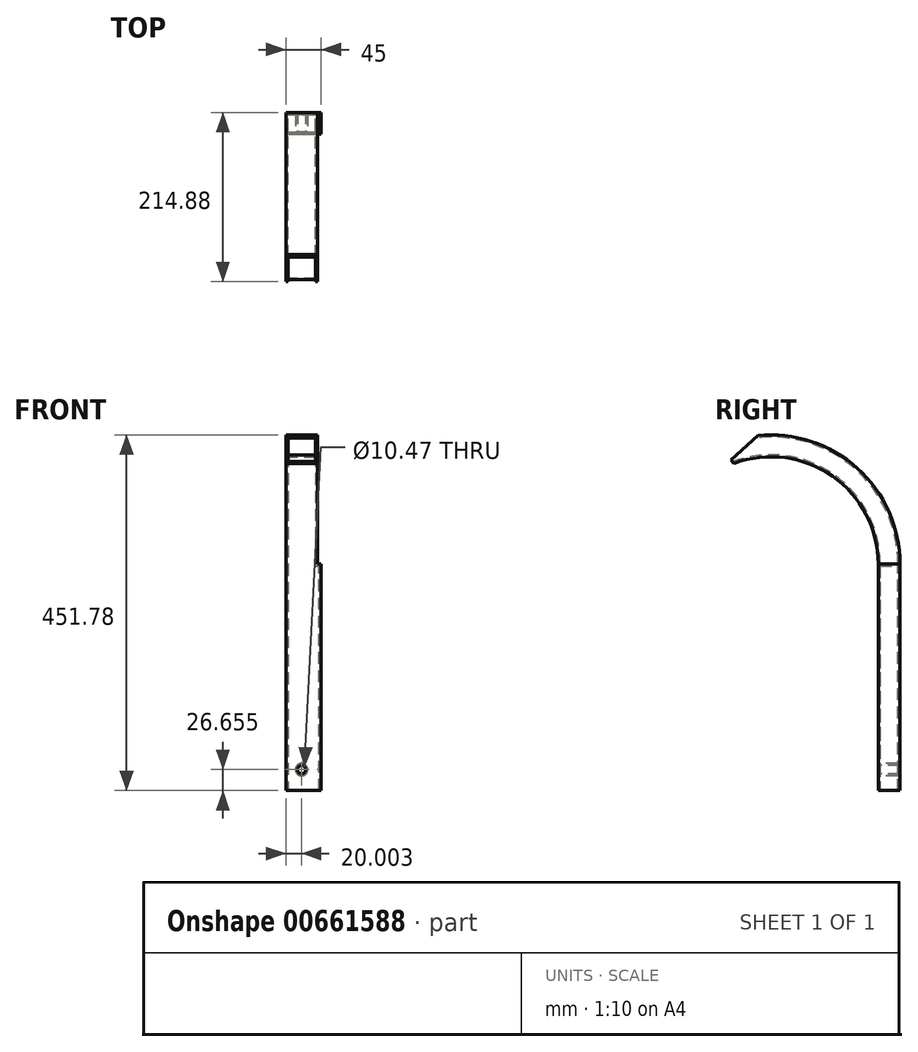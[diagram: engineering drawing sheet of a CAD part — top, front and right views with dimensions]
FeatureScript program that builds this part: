
annotation { "Feature Type Name" : "Feature", "Feature Type Description" : "" }
export const myFeature = defineFeature(function(context is Context, id is Id, definition is map)
    precondition{}
    {
        {
            var Q0;
            Q0=qCreatedBy(makeId("Front.planeOp"),FACE);
            var sketch = newSketch(context, id + "F0", { "sketchPlane" : qUnion([Q0])});
            skLineSegment(sketch, "E0.bottom", {"start": v(-20.98, -64.54) * mm, "end": v(59.02, -64.54) * mm});
            skLineSegment(sketch, "E0.top", {"start": v(-20.98, 335.46) * mm, "end": v(59.02, 335.46) * mm});
            skLineSegment(sketch, "E0.left", {"start": v(-20.98, -64.54) * mm, "end": v(-20.98, 335.46) * mm});
            skLineSegment(sketch, "E0.right", {"start": v(59.02, -64.54) * mm, "end": v(59.02, 335.46) * mm});
            skSolve(sketch);
        }
        {
            var Q0;
            Q0=makeQuery(id+"F0.imprint","IMPRINT",FACE,{"disambiguationData":[TD([[makeQuery(id+"F0.imprint","IMPRINT",EDGE,{"derivedFrom":sQuery(id+"F0.wireOp",EDGE,"E0.bottom")}),1.0]])]});
            extrude(context, id + "F1", {"entities" : qUnion([Q0]), "depth" : 300 * mm, "offsetDistance" : 25.4 * mm});
        }
        {
            var Q0;
            Q0=makeQuery(id+"F1.opExtrude","SWEPT_FACE",FACE,{"disambiguationData":[OSD([sQuery(id+"F0.wireOp",EDGE,"E0.left")])]});
            var sketch = newSketch(context, id + "F2", { "sketchPlane" : qUnion([Q0])});
            skLineSegment(sketch, "E1.1", {"start": v(300, -64.54) * mm, "end": v(0, -64.54) * mm});
            skLineSegment(sketch, "E2", {"start": v(40, -64.54) * mm, "end": v(40, 133.07) * mm});
            skLineSegment(sketch, "E3", {"start": v(218.3, 253.77) * mm, "end": v(248.43, 283.9) * mm});
            skPoint(sketch, "E4.orphan", {"position": v(0, 35.47) * mm});
            skArc(sketch, "E5.trimOffspring", {"start": v(218.3, 253.77) * mm, "mid": v(97.13, 240.73) * mm, "end": v(40, 133.07) * mm});
            skLineSegment(sketch, "E6.0", {"start": v(0, -64.54) * mm, "end": v(0, 133.07) * mm});
            skArc(sketch, "E6.1", {"start": v(248.43, 283.9) * mm, "mid": v(81.78, 278.39) * mm, "end": v(0, 133.07) * mm});
            skLineSegment(sketch, "E7.bottom", {"start": v(-14.01, 346.52) * mm, "end": v(324.59, 346.52) * mm});
            skLineSegment(sketch, "E7.top", {"start": v(-14.01, -79.57) * mm, "end": v(324.59, -79.57) * mm});
            skLineSegment(sketch, "E7.left", {"start": v(-14.01, 346.52) * mm, "end": v(-14.01, -79.57) * mm});
            skLineSegment(sketch, "E7.right", {"start": v(324.59, 346.52) * mm, "end": v(324.59, -79.57) * mm});
            skSolve(sketch);
        }
        {
            var Q0;
            {var subQ0=sQuery(id+"F2.wireOp",EDGE,"E2");Q0=makeQuery(id+"F2.imprint","IMPRINT",FACE,{"disambiguationData":[TD([[makeQuery(id+"F2.imprint","IMPRINT",EDGE,{"derivedFrom":subQ0}),-1.0]])]});}
            var Q1;
            {var subQ0=sQuery(id+"F2.wireOp",EDGE,"E6.0");Q1=makeQuery(id+"F2.imprint","IMPRINT",FACE,{"disambiguationData":[TD([[makeQuery(id+"F2.imprint","IMPRINT",EDGE,{"derivedFrom":subQ0}),1.0]])]});}
            extrude(context, id + "F3", {"entities" : qUnion([Q0, Q1]), "operationType" : NewBodyOperationType.REMOVE, "oppositeDirection" : true, "depth" : 108.97 * mm, "offsetDistance" : 25.4 * mm});
        }
        {
            var Q0;
            Q0=makeQuery(id+"F1.opExtrude","SWEPT_FACE",FACE,{"disambiguationData":[OSD([sQuery(id+"F0.wireOp",EDGE,"E0.bottom")])]});
            extrude(context, id + "F4", {"entities" : qUnion([Q0]), "operationType" : NewBodyOperationType.ADD, "depth" : 96.52 * mm, "offsetDistance" : 25.4 * mm});
        }
        {
            var Q0;
            {var subQ0=sQuery(id+"F2.wireOp",EDGE,"E2");var subQ1=sQuery(id+"F2.wireOp",EDGE,"E1.1");Q0=makeQuery(id+"F4.boolean.opBoolean","MERGE",FACE,{"derivedFrom":[makeQuery(id+"F3.boolean.opBoolean","COPY",FACE,{"derivedFrom":makeQuery(id+"F3.opExtrude","SWEPT_FACE",FACE,{"disambiguationData":[OSD([subQ0])]})}),makeQuery(id+"F4.opExtrude","SWEPT_FACE",FACE,{"disambiguationData":[OSD([subQ1,subQ0]),TDD([makeQuery(id+"F3.boolean.opBoolean","COPY",EDGE,{"derivedFrom":makeQuery(id+"F3.opExtrude","SWEPT_EDGE",EDGE,{"disambiguationData":[OSD([subQ1,subQ0])]})})])]})]});}
            var sketch = newSketch(context, id + "F5", { "sketchPlane" : qUnion([Q0])});
            skPoint(sketch, "E8.0", {"position": v(-20.98, -161.06) * mm});
            skPoint(sketch, "E9.0", {"position": v(59.02, -161.06) * mm});
            skLineSegment(sketch, "E10", {"start": v(19.02, -161.06) * mm, "end": v(19.02, 24.83) * mm});
            skCircle(sketch, "E11", {"center": v(19.02, -128.22) * mm, "radius": 5.23 * mm});
            skCircle(sketch, "E12", {"center": v(19.02, -73.97) * mm, "radius": 5.23 * mm});
            skSolve(sketch);
        }
        {
            var Q0;
            {var subQ0=sQuery(id+"F5.wireOp",EDGE,"E12");var subQ1=sQuery(id+"F5.wireOp",EDGE,"E10");var subQ2=makeQuery(id+"F5.imprint","INTERSECT",VERTEX,{"disambiguationData":[OD(0.0)],"derivedFrom":[subQ1,subQ0]});Q0=makeQuery(id+"F5.imprint","IMPRINT",FACE,{"disambiguationData":[TD([[makeQuery(id+"F5.imprint","IMPRINT",EDGE,{"disambiguationData":[TD([[subQ2,-1.0]])],"derivedFrom":subQ1}),-1.0]])]});}
            var Q1;
            {var subQ0=sQuery(id+"F5.wireOp",EDGE,"E12");var subQ1=sQuery(id+"F5.wireOp",EDGE,"E10");var subQ2=makeQuery(id+"F5.imprint","INTERSECT",VERTEX,{"disambiguationData":[OD(0.0)],"derivedFrom":[subQ1,subQ0]});Q1=makeQuery(id+"F5.imprint","IMPRINT",FACE,{"disambiguationData":[TD([[makeQuery(id+"F5.imprint","IMPRINT",EDGE,{"disambiguationData":[TD([[subQ2,-1.0]])],"derivedFrom":subQ1}),1.0]])]});}
            var Q2;
            {var subQ0=sQuery(id+"F5.wireOp",EDGE,"E11");var subQ1=sQuery(id+"F5.wireOp",EDGE,"E10");var subQ2=makeQuery(id+"F5.imprint","INTERSECT",VERTEX,{"disambiguationData":[OD(0.0)],"derivedFrom":[subQ1,subQ0]});Q2=makeQuery(id+"F5.imprint","IMPRINT",FACE,{"disambiguationData":[TD([[makeQuery(id+"F5.imprint","IMPRINT",EDGE,{"disambiguationData":[TD([[subQ2,-1.0]])],"derivedFrom":subQ1}),-1.0]])]});}
            var Q3;
            {var subQ0=sQuery(id+"F5.wireOp",EDGE,"E11");var subQ1=sQuery(id+"F5.wireOp",EDGE,"E10");var subQ2=makeQuery(id+"F5.imprint","INTERSECT",VERTEX,{"disambiguationData":[OD(0.0)],"derivedFrom":[subQ1,subQ0]});Q3=makeQuery(id+"F5.imprint","IMPRINT",FACE,{"disambiguationData":[TD([[makeQuery(id+"F5.imprint","IMPRINT",EDGE,{"disambiguationData":[TD([[subQ2,-1.0]])],"derivedFrom":subQ1}),1.0]])]});}
            extrude(context, id + "F6", {"entities" : qUnion([Q0, Q1, Q2, Q3]), "operationType" : NewBodyOperationType.REMOVE, "oppositeDirection" : true, "depth" : 46.23 * mm, "offsetDistance" : 25.4 * mm});
        }
        {
            var Q0;
            {var subQ0=sQuery(id+"F0.wireOp",EDGE,"E0.bottom");Q0=makeQuery(id+"F4.boolean.opBoolean","MERGE",FACE,{"derivedFrom":[makeQuery(id+"F1.opExtrude","CAP_FACE",FACE,{"disambiguationData":[OSD([subQ0,sQuery(id+"F0.wireOp",EDGE,"E0.top"),sQuery(id+"F0.wireOp",EDGE,"E0.left"),sQuery(id+"F0.wireOp",EDGE,"E0.right")])],"isStart":true}),makeQuery(id+"F4.opExtrude","SWEPT_FACE",FACE,{"disambiguationData":[OSD([subQ0])]})]});}
            var sketch = newSketch(context, id + "F7", { "sketchPlane" : qUnion([Q0])});
            skLineSegment(sketch, "E13", {"start": v(-19.02, -73.97) * mm, "end": v(-19.02, -175.55) * mm});
            skLineSegment(sketch, "E14", {"start": v(-19.02, -175.55) * mm, "end": v(5.98, -175.55) * mm});
            skLineSegment(sketch, "E15", {"start": v(5.98, -175.55) * mm, "end": v(5.98, 322.28) * mm});
            skLineSegment(sketch, "E16", {"start": v(5.98, 322.28) * mm, "end": v(-44.02, 322.28) * mm});
            skLineSegment(sketch, "E17", {"start": v(-44.02, 322.28) * mm, "end": v(-44.02, -175.55) * mm});
            skLineSegment(sketch, "E18", {"start": v(-44.02, -175.55) * mm, "end": v(-19.02, -175.55) * mm});
            skLineSegment(sketch, "E19.bottom", {"start": v(37.44, 348.2) * mm, "end": v(-87.02, 348.2) * mm});
            skLineSegment(sketch, "E19.top", {"start": v(37.44, -214.24) * mm, "end": v(-87.02, -214.24) * mm});
            skLineSegment(sketch, "E19.left", {"start": v(37.44, 348.2) * mm, "end": v(37.44, -214.24) * mm});
            skLineSegment(sketch, "E19.right", {"start": v(-87.02, 348.2) * mm, "end": v(-87.02, -214.24) * mm});
            skSolve(sketch);
        }
        {
            var Q0;
            {var subQ1=sQuery(id+"F0.wireOp",EDGE,"E0.bottom");var subQ4=sQuery(id+"F0.wireOp",EDGE,"E0.left");var subQ7=makeQuery(id+"F4.boolean.opBoolean","MERGE",EDGE,{"derivedFrom":[makeQuery(id+"F1.opExtrude","CAP_EDGE",EDGE,{"disambiguationData":[OSD([subQ4])],"isStart":true}),makeQuery(id+"F4.opExtrude","SWEPT_EDGE",EDGE,{"disambiguationData":[OSD([subQ1,subQ4])]})]});Q0=makeQuery(id+"F7.imprint","IMPRINT",FACE,{"disambiguationData":[TD([[makeQuery(id+"F7.imprint","IMPRINT",EDGE,{"derivedFrom":subQ7}),1.0]])]});}
            var Q1;
            {var subQ3=sQuery(id+"F0.wireOp",EDGE,"E0.bottom");var subQ6=sQuery(id+"F0.wireOp",EDGE,"E0.right");var subQ7=makeQuery(id+"F4.boolean.opBoolean","MERGE",EDGE,{"derivedFrom":[makeQuery(id+"F1.opExtrude","CAP_EDGE",EDGE,{"disambiguationData":[OSD([subQ6])],"isStart":true}),makeQuery(id+"F4.opExtrude","SWEPT_EDGE",EDGE,{"disambiguationData":[OSD([subQ3,subQ6])]})]});Q1=makeQuery(id+"F7.imprint","IMPRINT",FACE,{"disambiguationData":[TD([[makeQuery(id+"F7.imprint","IMPRINT",EDGE,{"derivedFrom":subQ7}),-1.0]])]});}
            var Q2;
            {var subQ9=sQuery(id+"F7.wireOp",EDGE,"E14");Q2=makeQuery(id+"F7.imprint","IMPRINT",FACE,{"disambiguationData":[TD([[makeQuery(id+"F7.imprint","IMPRINT",EDGE,{"derivedFrom":subQ9}),-1.0]])]});}
            extrude(context, id + "F8", {"entities" : qUnion([Q0, Q1, Q2]), "operationType" : NewBodyOperationType.REMOVE, "oppositeDirection" : true, "depth" : 391.16 * mm, "offsetDistance" : 25.4 * mm});
        }
        {
            var Q0;
            Q0=makeQuery(id+"F8.boolean.opBoolean","COPY",FACE,{"derivedFrom":makeQuery(id+"F8.opExtrude","SWEPT_FACE",FACE,{"disambiguationData":[OSD([sQuery(id+"F7.wireOp",EDGE,"E17")])]})});
            var sketch = newSketch(context, id + "F9", { "sketchPlane" : qUnion([Q0])});
            skLineSegment(sketch, "E20.0.0", {"start": v(-248.43, 283.9) * mm, "end": v(-218.3, 253.77) * mm});
            skArc(sketch, "E20.0.1", {"start": v(-218.3, 253.77) * mm, "mid": v(-97.13, 240.73) * mm, "end": v(-40, 133.07) * mm});
            skLineSegment(sketch, "E20.0.2", {"start": v(-40, 133.07) * mm, "end": v(-40, -161.06) * mm});
            skLineSegment(sketch, "E20.0.3", {"start": v(-40, -161.06) * mm, "end": v(0, -161.06) * mm});
            skLineSegment(sketch, "E20.0.4", {"start": v(0, -161.06) * mm, "end": v(0, 133.07) * mm});
            skArc(sketch, "E20.0.5", {"start": v(-248.43, 283.9) * mm, "mid": v(-81.78, 278.39) * mm, "end": v(0, 133.07) * mm});
            skArc(sketch, "E21.0", {"start": v(-245.5, 278.26) * mm, "mid": v(-85.07, 272.96) * mm, "end": v(-6.35, 133.07) * mm});
            skArc(sketch, "E22.0", {"start": v(-222.64, 264.61) * mm, "mid": v(-90.58, 250.4) * mm, "end": v(-28.32, 133.07) * mm});
            skLineSegment(sketch, "E23.0", {"start": v(-28.32, 133.07) * mm, "end": v(-28.32, -161.06) * mm});
            skLineSegment(sketch, "E24.0", {"start": v(-33.83, -154.88) * mm, "end": v(-6.17, -154.88) * mm});
            skArc(sketch, "E24.1", {"start": v(-237.95, 282.14) * mm, "mid": v(-81.38, 270.86) * mm, "end": v(-6.17, 133.07) * mm});
            skLineSegment(sketch, "E24.2", {"start": v(-237.95, 282.14) * mm, "end": v(-216.77, 260.96) * mm});
            skLineSegment(sketch, "E24.3", {"start": v(-6.17, -154.88) * mm, "end": v(-6.17, 133.07) * mm});
            skArc(sketch, "E24.4", {"start": v(-216.77, 260.96) * mm, "mid": v(-91.98, 244.68) * mm, "end": v(-33.83, 133.07) * mm});
            skLineSegment(sketch, "E24.5", {"start": v(-33.83, 133.07) * mm, "end": v(-33.83, -154.88) * mm});
            skSolve(sketch);
        }
        {
            var Q0;
            {var subQ2=sQuery(id+"F9.wireOp",EDGE,"E20.0.4");Q0=makeQuery(id+"F9.imprint","IMPRINT",FACE,{"disambiguationData":[TD([[makeQuery(id+"F9.imprint","IMPRINT",EDGE,{"derivedFrom":subQ2}),-1.0]])]});}
            var Q1;
            {var subQ13=sQuery(id+"F9.wireOp",EDGE,"E20.0.1");Q1=makeQuery(id+"F9.imprint","IMPRINT",FACE,{"disambiguationData":[TD([[makeQuery(id+"F9.imprint","IMPRINT",EDGE,{"derivedFrom":subQ13}),1.0]])]});}
            var Q2;
            {var subQ0=sQuery(id+"F9.wireOp",EDGE,"E24.4");Q2=makeQuery(id+"F9.imprint","IMPRINT",FACE,{"disambiguationData":[TD([[makeQuery(id+"F9.imprint","IMPRINT",EDGE,{"derivedFrom":subQ0}),1.0]])]});}
            extrude(context, id + "F10", {"entities" : qUnion([Q0, Q1, Q2]), "operationType" : NewBodyOperationType.REMOVE, "oppositeDirection" : true, "depth" : 73.66 * mm, "offsetDistance" : 25.4 * mm});
        }
        {
            var Q0;
            Q0=makeQuery(id+"F10.boolean.opBoolean","COPY",FACE,{"derivedFrom":makeQuery(id+"F10.opExtrude","SWEPT_FACE",FACE,{"disambiguationData":[OSD([sQuery(id+"F9.wireOp",EDGE,"E24.3")])]})});
            var sketch = newSketch(context, id + "F11", { "sketchPlane" : qUnion([Q0])});
            skLineSegment(sketch, "E25", {"start": v(-19.02, -128.22) * mm, "end": v(0.98, -128.22) * mm});
            skLineSegment(sketch, "E26", {"start": v(-19.02, -73.97) * mm, "end": v(-39.02, -73.97) * mm});
            skLineSegment(sketch, "E27.bottom", {"start": v(0.98, -172.53) * mm, "end": v(-39.02, -172.53) * mm});
            skLineSegment(sketch, "E27.top", {"start": v(0.98, 334.83) * mm, "end": v(-39.02, 334.83) * mm});
            skLineSegment(sketch, "E27.left", {"start": v(0.98, -172.53) * mm, "end": v(0.98, 334.83) * mm});
            skLineSegment(sketch, "E27.right", {"start": v(-39.02, -172.53) * mm, "end": v(-39.02, 334.83) * mm});
            skLineSegment(sketch, "E28.bottom", {"start": v(-65, 352.61) * mm, "end": v(27.95, 352.61) * mm});
            skLineSegment(sketch, "E28.top", {"start": v(-65, -187.26) * mm, "end": v(27.95, -187.26) * mm});
            skLineSegment(sketch, "E28.left", {"start": v(-65, 352.61) * mm, "end": v(-65, -187.26) * mm});
            skLineSegment(sketch, "E28.right", {"start": v(27.95, 352.61) * mm, "end": v(27.95, -187.26) * mm});
            skSolve(sketch);
        }
        {
            var Q0;
            {var subQ0=sQuery(id+"F9.wireOp",EDGE,"E24.3");var subQ1=makeQuery(id+"F10.boolean.opBoolean","INTERSECT",EDGE,{"derivedFrom":[makeQuery(id+"F8.boolean.opBoolean","COPY",FACE,{"derivedFrom":makeQuery(id+"F8.opExtrude","SWEPT_FACE",FACE,{"disambiguationData":[OSD([sQuery(id+"F7.wireOp",EDGE,"E15")])]})}),makeQuery(id+"F10.opExtrude","SWEPT_FACE",FACE,{"disambiguationData":[OSD([subQ0])]})]});Q0=makeQuery(id+"F11.imprint","IMPRINT",FACE,{"disambiguationData":[TD([[makeQuery(id+"F11.imprint","IMPRINT",EDGE,{"derivedFrom":subQ1}),-1.0]])]});}
            var Q1;
            {var subQ5=sQuery(id+"F11.wireOp",EDGE,"E27.bottom");Q1=makeQuery(id+"F11.imprint","IMPRINT",FACE,{"disambiguationData":[TD([[makeQuery(id+"F11.imprint","IMPRINT",EDGE,{"derivedFrom":subQ5}),1.0]])]});}
            var Q2;
            {var subQ0=sQuery(id+"F9.wireOp",EDGE,"E24.3");var subQ1=makeQuery(id+"F10.boolean.opBoolean","COPY",EDGE,{"derivedFrom":makeQuery(id+"F10.opExtrude","CAP_EDGE",EDGE,{"disambiguationData":[OSD([subQ0])],"isStart":true})});Q2=makeQuery(id+"F11.imprint","IMPRINT",FACE,{"disambiguationData":[TD([[makeQuery(id+"F11.imprint","IMPRINT",EDGE,{"derivedFrom":subQ1}),-1.0]])]});}
            extrude(context, id + "F12", {"entities" : qUnion([Q0, Q1, Q2]), "operationType" : NewBodyOperationType.REMOVE, "oppositeDirection" : true, "depth" : 243.84 * mm, "offsetDistance" : 25.4 * mm});
        }
        {
            var Q0;
            Q0=makeQuery(id+"F10.boolean.opBoolean","COPY",FACE,{"derivedFrom":makeQuery(id+"F10.opExtrude","SWEPT_FACE",FACE,{"disambiguationData":[OSD([sQuery(id+"F9.wireOp",EDGE,"E24.2")])]})});
            var Q1;
            Q1=makeQuery(id+"F10.boolean.opBoolean","COPY",FACE,{"derivedFrom":makeQuery(id+"F10.opExtrude","SWEPT_FACE",FACE,{"disambiguationData":[OSD([sQuery(id+"F9.wireOp",EDGE,"E24.0")])]})});
            shell(context, id + "F13", {"entities" : qUnion([Q0, Q1]), "thickness" : 2.54 * mm});
        }
        {
            var Q0;
            Q0=makeQuery(id+"F12.boolean.opBoolean","COPY",FACE,{"derivedFrom":makeQuery(id+"F12.opExtrude","SWEPT_FACE",FACE,{"disambiguationData":[OSD([sQuery(id+"F11.wireOp",EDGE,"E27.right")])]})});
            var sketch = newSketch(context, id + "F14", { "sketchPlane" : qUnion([Q0])});
            skLineSegment(sketch, "E29.0.0", {"start": v(-28.32, -154.88) * mm, "end": v(-6.17, -154.88) * mm});
            skLineSegment(sketch, "E29.0.1", {"start": v(-6.17, -154.88) * mm, "end": v(-6.17, 133.07) * mm});
            skArc(sketch, "E29.0.2", {"start": v(-6.17, 133.07) * mm, "mid": v(-81.38, 270.86) * mm, "end": v(-237.95, 282.14) * mm});
            skLineSegment(sketch, "E29.0.3", {"start": v(-237.95, 282.14) * mm, "end": v(-221.05, 265.24) * mm});
            skArc(sketch, "E29.0.4", {"start": v(-221.05, 265.24) * mm, "mid": v(-89.87, 249.92) * mm, "end": v(-28.32, 133.07) * mm});
            skLineSegment(sketch, "E29.0.5", {"start": v(-28.32, 133.07) * mm, "end": v(-28.32, -154.88) * mm});
            skLineSegment(sketch, "E30", {"start": v(-178.62, 303.24) * mm, "end": v(-221.05, 265.24) * mm});
            skSolve(sketch);
        }
        {
            var Q0;
            {var subQ0=sQuery(id+"F14.wireOp",EDGE,"E29.0.3");Q0=makeQuery(id+"F14.imprint","IMPRINT",FACE,{"disambiguationData":[TD([[makeQuery(id+"F14.imprint","IMPRINT",EDGE,{"derivedFrom":subQ0}),1.0]])]});}
            extrude(context, id + "F15", {"entities" : qUnion([Q0]), "operationType" : NewBodyOperationType.REMOVE, "oppositeDirection" : true, "depth" : 56.4 * mm, "offsetDistance" : 25.4 * mm});
        }
    });
